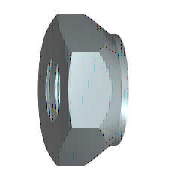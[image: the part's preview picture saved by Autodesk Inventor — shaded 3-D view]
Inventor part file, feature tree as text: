
AUTODESK INVENTOR PART (.ipt)
format: ipt  version: 2017 (Build 210142000, 142)  size: 185,344 bytes
history: native  units: mm (DEFAULTED — no unit token found)
features: sketch x3, hole x1, chamfer x1, other x1, plane x1
ambient origin geometry x7: Origin, YZ Plane, XZ Plane, X Axis, Y Axis, Z Axis, Center Point
bodies: Solid1 (feature_tree), Body (feature_tree)
feature tree (7):
  hole  "Thread"  [1 undecoded]
  chamfer  "Chamfer3"  Distance=8.0mm
  other  "Work Axis1"
  plane  "Work Plane1"
  sketch  "Sketch1"  dims[d0=9.237604mm d1=5.3mm]
  sketch  "Sketch3"  dims[d3=30.0deg d5=8.0mm d6=6.8mm d7=90.0deg d8=8.726646mm d9=2.7mm d24=4.134mm d25=6.0mm d26=4.0mm d27=2.0mm d28=14.3117mm d29=8.0mm d30=20.594885mm d10=0.433013mm d11=30.0deg d12=0.433013mm d13=30.0deg d14=0.0mm d38=0.0mm d39=0.433013mm d40=0.433013mm d41=0.0mm d42=0.0mm]
  sketch  "Sketch2"  dims[d2=0.0mm]
note: 1 required parameter value undecoded (feature->parameter linkage not recoverable at this tier; creation-order binding heuristic only, values carry confidence <= 0.55)
